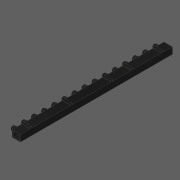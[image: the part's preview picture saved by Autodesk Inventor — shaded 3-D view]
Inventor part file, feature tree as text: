
AUTODESK INVENTOR PART (.ipt)
format: ipt  version: 2020 (Build 240168000, 168)  size: 293,888 bytes
history: native  units: in
note: dims shown in document units (in); Inventor stores cm internally (conversion verified against a paired STEP export)
features: other x6, extrude x3, pattern_linear x1, projected_geometry x1
ambient origin geometry x8: Origin, YZ Plane, XZ Plane, XY Plane, X Axis, Y Axis, Z Axis, Center Point
bodies: Solid1 (feature_tree)
feature tree (11):
  extrude  "Box"  Depth=0.063in
  other  "Fitting Plane"
  other  "Fitting"
  extrude  "Fitting Entrance"  Depth=0.0315in
  pattern_linear  "Channel Repetition"  Spacing1=0.0315in  [1 undecoded]
  extrude  "Tabs"  Depth=0.4882in TaperAngle=0.0deg
  other  "Box Sketch"
  other  "Fitting Sketch"
  other  "Fitting Entrance Sketch"
  projected_geometry  "Projected Loop1"
  other  "Tab Sketch"
note: 1 required parameter value undecoded (feature->parameter linkage not recoverable at this tier; creation-order binding heuristic only, values carry confidence <= 0.55)
